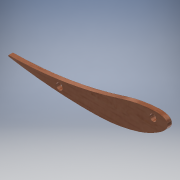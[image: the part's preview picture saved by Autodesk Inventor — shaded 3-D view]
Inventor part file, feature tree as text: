
AUTODESK INVENTOR PART (.ipt)
format: ipt  version: 2018 (Build 220112000, 112)  size: 140,288 bytes
history: native  units: mm
features: extrude x2, sketch x2, other x1, projected_geometry x1
ambient origin geometry x8: Origin, YZ Plane, XZ Plane, XY Plane, X Axis, Y Axis, Z Axis, Center Point
bodies: Body1 (feature_tree)
feature tree (6):
  extrude  "押し出し1"  Depth=4.0mm TaperAngle=0.0deg
  extrude  "押し出し2"  Depth=6.0mm
  other  "厚み1"
  sketch  "スケッチ1"
  projected_geometry  "投影ループ1"
  sketch  "スケッチ2"
